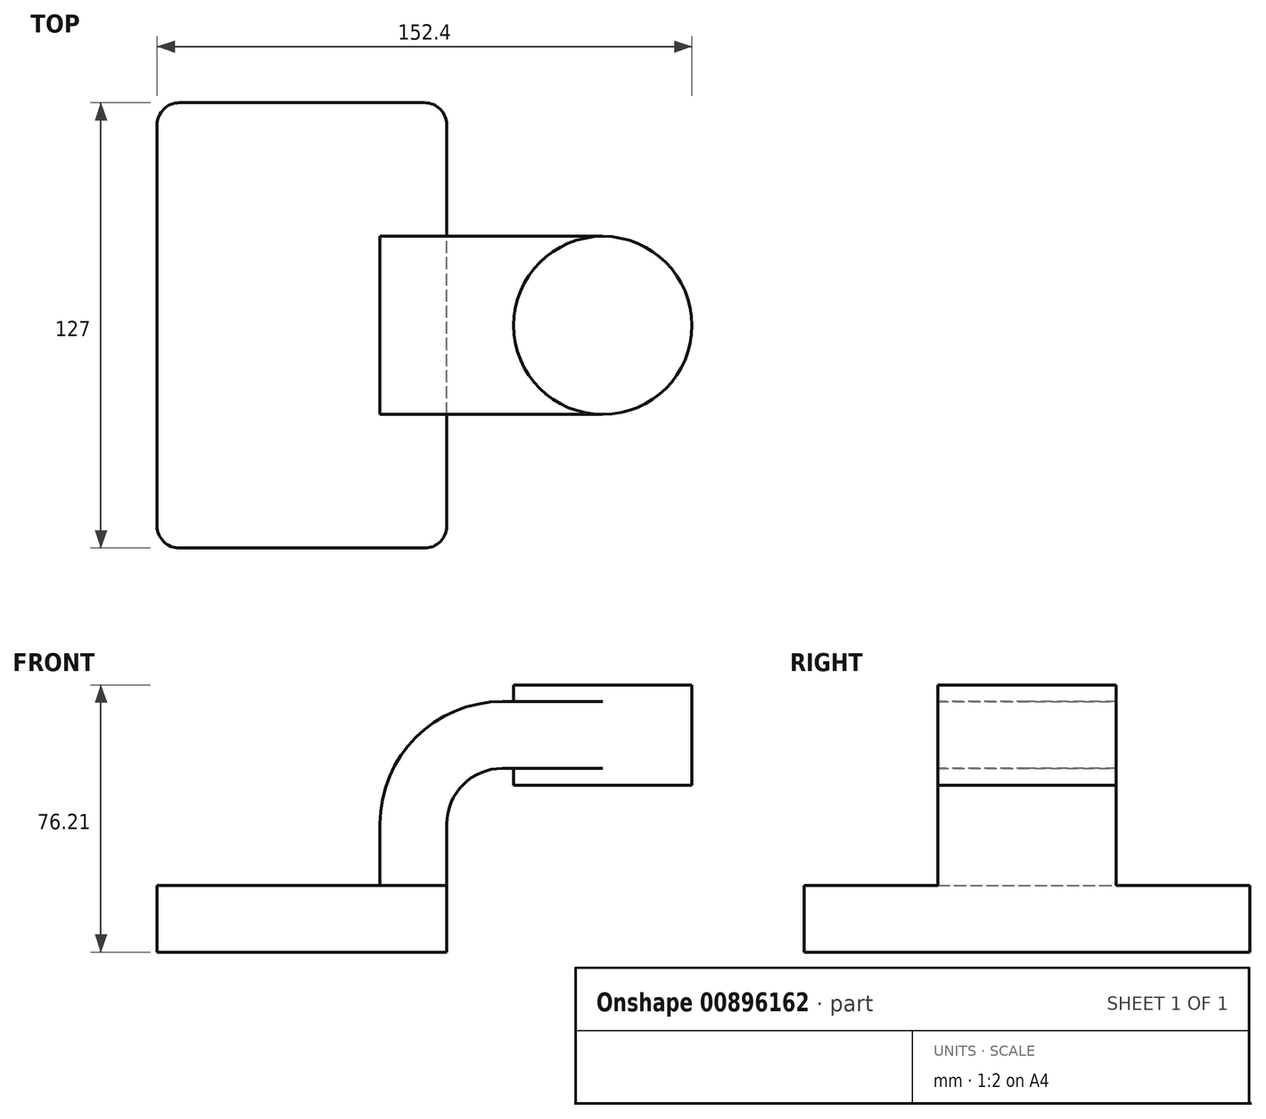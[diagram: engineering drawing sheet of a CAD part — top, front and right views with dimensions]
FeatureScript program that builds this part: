
annotation { "Feature Type Name" : "Feature", "Feature Type Description" : "" }
export const myFeature = defineFeature(function(context is Context, id is Id, definition is map)
    precondition{}
    {
        {
            var Q0;
            Q0=qCreatedBy(makeId("Front.planeOp"),FACE);
            var sketch = newSketch(context, id + "F0", { "sketchPlane" : qUnion([Q0])});
            skLineSegment(sketch, "E0.bottom", {"start": v(41.27, 9.53) * mm, "end": v(-41.28, 9.53) * mm});
            skLineSegment(sketch, "E0.top", {"start": v(41.28, -9.53) * mm, "end": v(-41.27, -9.53) * mm});
            skLineSegment(sketch, "E0.left", {"start": v(41.28, 9.53) * mm, "end": v(41.28, -9.53) * mm});
            skLineSegment(sketch, "E0.right", {"start": v(-41.28, 9.53) * mm, "end": v(-41.28, -9.53) * mm});
            skPoint(sketch, "E0.middle", {"position": v(0, 0) * mm});
            skLineSegment(sketch, "E1.bottom", {"start": v(111.12, 38.1) * mm, "end": v(60.32, 38.1) * mm});
            skLineSegment(sketch, "E1.top", {"start": v(111.12, 66.68) * mm, "end": v(60.32, 66.68) * mm});
            skLineSegment(sketch, "E1.left", {"start": v(111.12, 38.1) * mm, "end": v(111.12, 66.68) * mm});
            skLineSegment(sketch, "E1.right", {"start": v(60.32, 38.1) * mm, "end": v(60.32, 66.68) * mm});
            skPoint(sketch, "E1.middle", {"position": v(85.72, 52.39) * mm});
            skLineSegment(sketch, "E2", {"start": v(41.27, 9.53) * mm, "end": v(41.27, 27) * mm});
            skArc(sketch, "E3", {"start": v(41.27, 27) * mm, "mid": v(45.92, 38.23) * mm, "end": v(57.15, 42.88) * mm});
            skLineSegment(sketch, "E4", {"start": v(57.15, 42.88) * mm, "end": v(85.72, 42.88) * mm});
            skLineSegment(sketch, "E5.0", {"start": v(57.15, 61.93) * mm, "end": v(85.72, 61.93) * mm});
            skArc(sketch, "E5.1", {"start": v(22.22, 27) * mm, "mid": v(32.45, 51.7) * mm, "end": v(57.15, 61.93) * mm});
            skLineSegment(sketch, "E5.2", {"start": v(22.22, 9.52) * mm, "end": v(22.22, 27) * mm});
            skFitSpline(sketch, "E6", {"points": [v(-41.28, 9.53) * mm, v(57.15, 61.93) * mm], "startDerivative": vector(1.89, 72.31) * mm, "endDerivative": vector(68.61, 0) * mm});
            skLineSegment(sketch, "E7", {"start": v(85.72, 38.1) * mm, "end": v(85.72, 66.68) * mm});
            skSolve(sketch);
        }
        {
            var Q0;
            Q0=makeQuery(id+"F0.imprint","IMPRINT",FACE,{"disambiguationData":[TD([[makeQuery(id+"F0.imprint","IMPRINT",EDGE,{"derivedFrom":sQuery(id+"F0.wireOp",EDGE,"E5.1")}),1.0]])]});
            extrude(context, id + "F1", {"entities" : qUnion([Q0]), "endBound" : BoundingType.SYMMETRIC, "depth" : 15.88 * mm, "offsetDistance" : 25.4 * mm});
        }
        {
            var Q0;
            Q0=makeQuery(id+"F0.imprint","IMPRINT",FACE,{"disambiguationData":[TD([[makeQuery(id+"F0.imprint","IMPRINT",EDGE,{"derivedFrom":sQuery(id+"F0.wireOp",EDGE,"E0.top")}),-1.0]])]});
            extrude(context, id + "F2", {"entities" : qUnion([Q0]), "operationType" : NewBodyOperationType.ADD, "endBound" : BoundingType.SYMMETRIC, "depth" : 127 * mm, "offsetDistance" : 25.4 * mm});
        }
        {
            var Q0;
            {var subQ1=sQuery(id+"F0.wireOp",EDGE,"E2");Q0=makeQuery(id+"F0.imprint","IMPRINT",FACE,{"disambiguationData":[TD([[makeQuery(id+"F0.imprint","IMPRINT",EDGE,{"derivedFrom":subQ1}),1.0]])]});}
            var Q1;
            {var subQ0=sQuery(id+"F0.wireOp",EDGE,"E4");var subQ1=sQuery(id+"F0.wireOp",EDGE,"E1.right");var subQ2=makeQuery(id+"F0.imprint","INTERSECT",VERTEX,{"derivedFrom":[subQ1,subQ0]});Q1=makeQuery(id+"F0.imprint","IMPRINT",FACE,{"disambiguationData":[TD([[makeQuery(id+"F0.imprint","IMPRINT",EDGE,{"disambiguationData":[TD([[subQ2,-1.0]])],"derivedFrom":subQ1}),-1.0]])]});}
            extrude(context, id + "F3", {"entities" : qUnion([Q0, Q1]), "operationType" : NewBodyOperationType.ADD, "endBound" : BoundingType.SYMMETRIC, "depth" : 50.8 * mm, "offsetDistance" : 25.4 * mm});
        }
        {
            var Q0;
            Q0=makeQuery(id+"F2.opExtrude","CAP_EDGE",EDGE,{"disambiguationData":[OSD([sQuery(id+"F0.wireOp",EDGE,"E0.left")])],"isStart":false});
            var Q1;
            Q1=makeQuery(id+"F2.opExtrude","CAP_EDGE",EDGE,{"disambiguationData":[OSD([sQuery(id+"F0.wireOp",EDGE,"E0.right")])],"isStart":false});
            var Q2;
            Q2=makeQuery(id+"F2.opExtrude","CAP_EDGE",EDGE,{"disambiguationData":[OSD([sQuery(id+"F0.wireOp",EDGE,"E0.right")])],"isStart":true});
            var Q3;
            Q3=makeQuery(id+"F2.opExtrude","CAP_EDGE",EDGE,{"disambiguationData":[OSD([sQuery(id+"F0.wireOp",EDGE,"E0.left")])],"isStart":true});
            fillet(context, id + "F4", {"entities" : qUnion([Q0, Q1, Q2, Q3]), "radius" : 6.35 * mm, "tangentPropagation" : true, "allowEdgeOverflow" : false});
        }
        {
            var Q0;
            {var subQ0=sQuery(id+"F0.wireOp",EDGE,"E1.left");Q0=makeQuery(id+"F0.imprint","IMPRINT",FACE,{"disambiguationData":[TD([[makeQuery(id+"F0.imprint","IMPRINT",EDGE,{"derivedFrom":subQ0}),1.0]])]});}
            var Q1;
            Q1=sQuery(id+"F0.wireOp",EDGE,"E7");
            revolve(context, id + "F5", {"operationType" : NewBodyOperationType.ADD, "surfaceOperationType" : NewSurfaceOperationType.NEW, "entities" : qUnion([Q0]), "axis" : qUnion([Q1]), "revolveType" : RevolveType.FULL});
        }
    });
